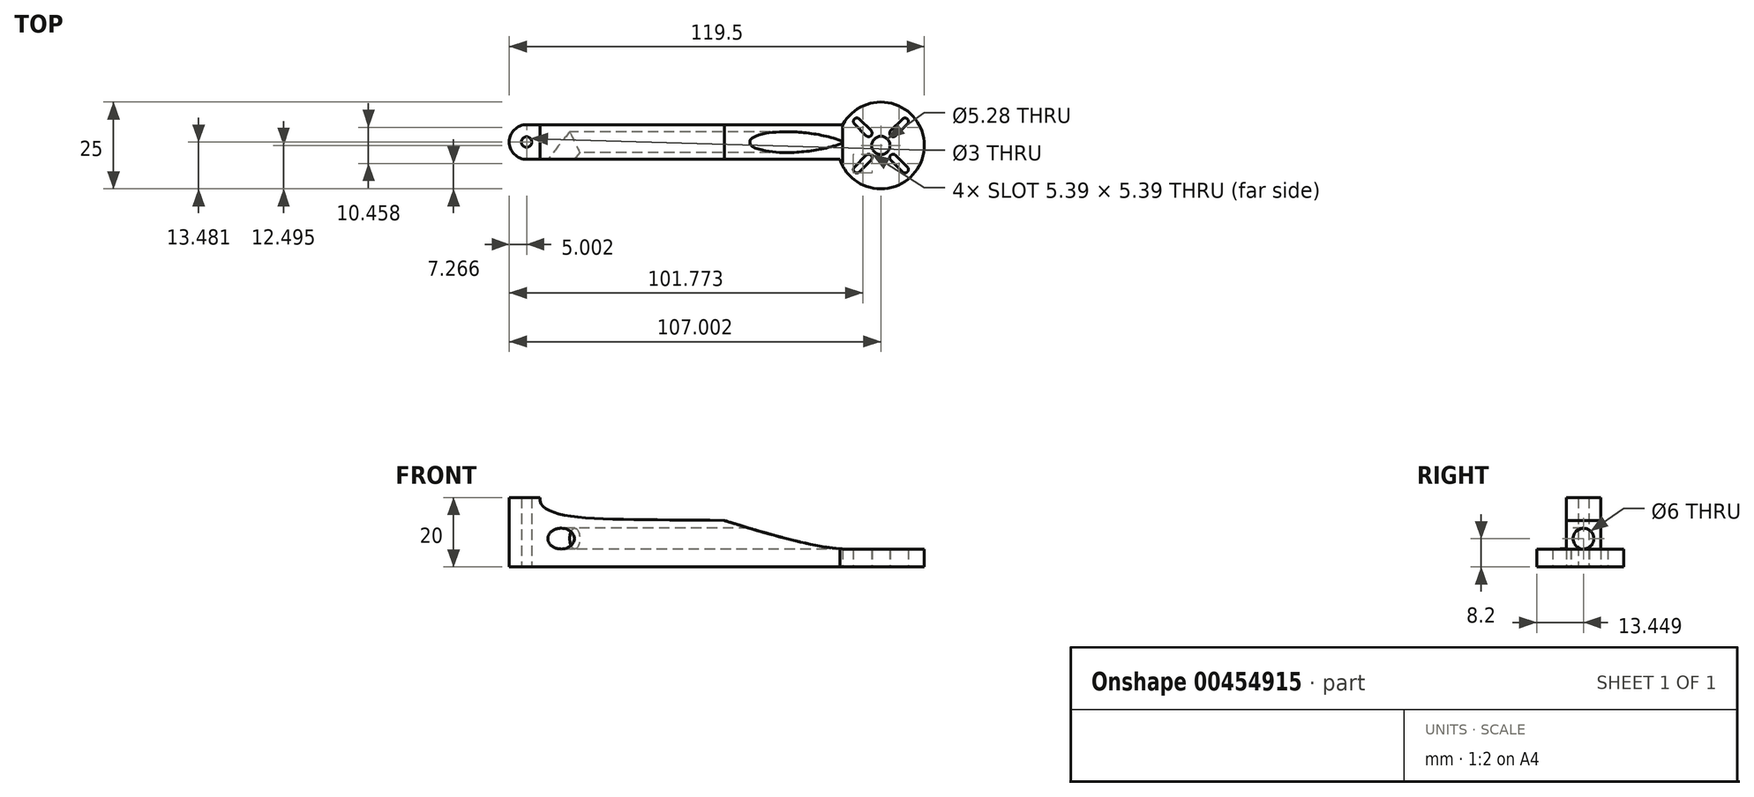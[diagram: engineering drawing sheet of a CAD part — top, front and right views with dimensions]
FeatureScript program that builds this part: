
annotation { "Feature Type Name" : "Feature", "Feature Type Description" : "" }
export const myFeature = defineFeature(function(context is Context, id is Id, definition is map)
    precondition{}
    {
        {
            var Q0;
            Q0=qCreatedBy(makeId("Top.planeOp"),FACE);
            var sketch = newSketch(context, id + "F0", { "sketchPlane" : qUnion([Q0])});
            skLineSegment(sketch, "E0", {"start": v(-139.16, 59.15) * mm, "end": v(-37.16, 59.15) * mm, "construction": true});
            skArc(sketch, "E1", {"start": v(-48.13, 53.17) * mm, "mid": v(-24.7, 60.23) * mm, "end": v(-49, 63.17) * mm});
            skLineSegment(sketch, "E2", {"start": v(-139.16, 63.17) * mm, "end": v(-49, 63.17) * mm});
            skLineSegment(sketch, "E3", {"start": v(-139.16, 53.17) * mm, "end": v(-48.13, 53.17) * mm});
            skCircle(sketch, "E4", {"center": v(-37.16, 59.15) * mm, "radius": 2.64 * mm});
            skArc(sketch, "E5.0.startCap", {"start": v(-44.79, 65.37) * mm, "mid": v(-44.79, 66.78) * mm, "end": v(-43.37, 66.78) * mm});
            skArc(sketch, "E5.0.endCap", {"start": v(-39.99, 63.4) * mm, "mid": v(-39.99, 61.98) * mm, "end": v(-41.4, 61.98) * mm});
            skLineSegment(sketch, "E5.0.left", {"start": v(-43.37, 66.78) * mm, "end": v(-39.99, 63.4) * mm});
            skLineSegment(sketch, "E5.0.right", {"start": v(-44.79, 65.37) * mm, "end": v(-41.4, 61.98) * mm});
            skLineSegment(sketch, "E6", {"start": v(-37.16, 59.15) * mm, "end": v(-37.16, 66.76) * mm, "construction": true});
            skArc(sketch, "E7.MirrorCS", {"start": v(-29.53, 65.37) * mm, "mid": v(-29.53, 66.78) * mm, "end": v(-30.94, 66.78) * mm});
            skArc(sketch, "E8.MirrorCS", {"start": v(-34.33, 63.4) * mm, "mid": v(-34.33, 61.98) * mm, "end": v(-32.92, 61.98) * mm});
            skLineSegment(sketch, "E9.MirrorCS", {"start": v(-29.53, 65.37) * mm, "end": v(-32.92, 61.98) * mm});
            skLineSegment(sketch, "E10.MirrorCS", {"start": v(-30.94, 66.78) * mm, "end": v(-34.33, 63.4) * mm});
            skLineSegment(sketch, "E11.MirrorCS", {"start": v(-30.94, 51.52) * mm, "end": v(-34.33, 54.91) * mm});
            skArc(sketch, "E12.MirrorCS", {"start": v(-29.53, 52.94) * mm, "mid": v(-29.53, 51.52) * mm, "end": v(-30.94, 51.52) * mm});
            skLineSegment(sketch, "E13.MirrorCS", {"start": v(-29.53, 52.94) * mm, "end": v(-32.92, 56.33) * mm});
            skArc(sketch, "E14.MirrorCS", {"start": v(-34.33, 54.91) * mm, "mid": v(-34.33, 56.33) * mm, "end": v(-32.92, 56.33) * mm});
            skLineSegment(sketch, "E15.MirrorCS", {"start": v(-44.79, 52.94) * mm, "end": v(-41.4, 56.33) * mm});
            skLineSegment(sketch, "E16.MirrorCS", {"start": v(-43.37, 51.52) * mm, "end": v(-39.99, 54.91) * mm});
            skArc(sketch, "E17.MirrorCS", {"start": v(-39.99, 54.91) * mm, "mid": v(-39.99, 56.33) * mm, "end": v(-41.4, 56.33) * mm});
            skArc(sketch, "E18.MirrorCS", {"start": v(-44.79, 52.94) * mm, "mid": v(-44.79, 51.52) * mm, "end": v(-43.37, 51.52) * mm});
            skLineSegment(sketch, "E19", {"start": v(-37.16, 59.15) * mm, "end": v(-44.76, 66.76) * mm, "construction": true});
            skLineSegment(sketch, "E20", {"start": v(-139.16, 53.17) * mm, "end": v(-139.16, 63.17) * mm, "construction": true});
            skPoint(sketch, "E21", {"position": v(-139.16, 58.17) * mm});
            skArc(sketch, "E22", {"start": v(-139.16, 53.17) * mm, "mid": v(-144.16, 58.17) * mm, "end": v(-139.16, 63.17) * mm});
            skCircle(sketch, "E23", {"center": v(-139.16, 58.17) * mm, "radius": 1.5 * mm});
            skSolve(sketch);
        }
        {
            var Q0;
            Q0=qSketchRegion(id+"F0",true);
            extrude(context, id + "F1", {"entities" : qUnion([Q0]), "depth" : 20 * mm});
        }
        {
            var Q0;
            Q0=makeQuery(id+"F1.opExtrude","SWEPT_FACE",FACE,{"disambiguationData":[OSD([sQuery(id+"F0.wireOp",EDGE,"E3")])]});
            var sketch = newSketch(context, id + "F2", { "sketchPlane" : qUnion([Q0])});
            skFitSpline(sketch, "E24", {"points": [v(-48.13, 5.2) * mm, v(-101.02, 20) * mm], "startDerivative": vector(-37.65, 1.6) * mm, "endDerivative": vector(-23.18, 9.57) * mm});
            skLineSegment(sketch, "E25", {"start": v(-48.13, 5.2) * mm, "end": v(66.1, 5.2) * mm});
            skLineSegment(sketch, "E26", {"start": v(66.1, 5.2) * mm, "end": v(64.34, 23.02) * mm});
            skLineSegment(sketch, "E27", {"start": v(64.34, 23.02) * mm, "end": v(-14.17, 23.97) * mm});
            skLineSegment(sketch, "E28", {"start": v(-14.17, 23.97) * mm, "end": v(-21.08, 20) * mm});
            skLineSegment(sketch, "E29", {"start": v(-48.13, 13.43) * mm, "end": v(-82.25, 13.43) * mm});
            skLineSegment(sketch, "E30", {"start": v(-48.13, 13.43) * mm, "end": v(-48.13, 24.34) * mm});
            skLineSegment(sketch, "E31", {"start": v(-48.13, 24.34) * mm, "end": v(-21.08, 20) * mm});
            skSolve(sketch);
        }
        {
            var Q0;
            Q0=qSketchRegion(id+"F2",true);
            extrude(context, id + "F3", {"entities" : qUnion([Q0]), "operationType" : NewBodyOperationType.REMOVE, "oppositeDirection" : true, "depth" : 25 * mm, "hasSecondDirection" : true, "secondDirectionOppositeDirection" : false, "secondDirectionDepth" : 25 * mm});
        }
        {
            var Q0;
            Q0=makeQuery(id+"F3.boolean.opBoolean","COPY",FACE,{"derivedFrom":makeQuery(id+"F3.opExtrude","SWEPT_FACE",FACE,{"disambiguationData":[OSD([sQuery(id+"F2.wireOp",EDGE,"E25")])]})});
            var sketch = newSketch(context, id + "F4", { "sketchPlane" : qUnion([Q0])});
            skLineSegment(sketch, "E32", {"start": v(-86.71, 58.17) * mm, "end": v(-61.2, 58.17) * mm});
            skLineSegment(sketch, "E33", {"start": v(-86.71, 58.17) * mm, "end": v(-125.32, 58.17) * mm});
            skLineSegment(sketch, "E34", {"start": v(-125.32, 58.17) * mm, "end": v(-138.96, 75.4) * mm});
            skSolve(sketch);
        }
        {
            var Q0;
            Q0=makeQuery(id+"F3.boolean.opBoolean","COPY",EDGE,{"derivedFrom":makeQuery(id+"F3.opExtrude","SWEPT_EDGE",EDGE,{"disambiguationData":[OSD([sQuery(id+"F0.wireOp",EDGE,"E1"),sQuery(id+"F0.wireOp",EDGE,"E3"),sQuery(id+"F2.wireOp",EDGE,"E24"),sQuery(id+"F2.wireOp",EDGE,"E25")])]})});
            cPlane(context, id + "F5", {"entities" : qUnion([Q0]), "cplaneType" : CPlaneType.LINE_ANGLE, "offset" : 25 * mm, "angle" : 90 * degree, "width" : 150 * mm, "height" : 150 * mm});
        }
        {
            var Q0;
            Q0=qCreatedBy(id+"F5.planeOp",FACE);
            var sketch = newSketch(context, id + "F6", { "sketchPlane" : qUnion([Q0])});
            skLineSegment(sketch, "E35.0", {"start": v(65.14, 5.2) * mm, "end": v(53.17, 5.2) * mm, "construction": true});
            skCircle(sketch, "E36", {"center": v(58.2, 8.2) * mm, "radius": 3 * mm});
            skSolve(sketch);
        }
        {
            var Q0;
            Q0=qSketchRegion(id+"F6",true);
            var Q1;
            Q1=qConstructionFilter(qBodyType(qCreatedBy(id+"F4",EDGE),BodyType.WIRE),ConstructionObject.NO);
            sweep(context, id + "F7", {"operationType" : NewBodyOperationType.REMOVE, "profiles" : qUnion([Q0]), "path" : qUnion([Q1])});
        }
        {
            var Q0;
            Q0=makeQuery(id+"F1.opExtrude","SWEPT_FACE",FACE,{"disambiguationData":[OSD([sQuery(id+"F0.wireOp",EDGE,"E3")])]});
            var sketch = newSketch(context, id + "F8", { "sketchPlane" : qUnion([Q0])});
            skPoint(sketch, "E37.0", {"position": v(-82.25, 13.43) * mm});
            skFitSpline(sketch, "E38", {"points": [v(-82.25, 13.43) * mm, v(-135.35, 20) * mm], "startDerivative": vector(-96, 1.58) * mm, "endDerivative": vector(1.3, 22.57) * mm});
            skLineSegment(sketch, "E39", {"start": v(-82.25, 13.43) * mm, "end": v(-32.97, 11.71) * mm});
            skLineSegment(sketch, "E40", {"start": v(-32.97, 11.71) * mm, "end": v(-32.97, 37.38) * mm});
            skLineSegment(sketch, "E41", {"start": v(-32.97, 37.38) * mm, "end": v(-135.35, 20) * mm});
            skSolve(sketch);
        }
        {
            var Q0;
            Q0=qSketchRegion(id+"F8",true);
            extrude(context, id + "F9", {"entities" : qUnion([Q0]), "operationType" : NewBodyOperationType.REMOVE, "oppositeDirection" : true, "depth" : 25 * mm});
        }
        {
            var Q0;
            Q0=makeQuery(id+"F1.opExtrude","SWEPT_BODY",BODY,{"disambiguationData":[OSD([sQuery(id+"F0.wireOp",EDGE,"E1"),sQuery(id+"F0.wireOp",EDGE,"E2"),sQuery(id+"F0.wireOp",EDGE,"E3"),sQuery(id+"F0.wireOp",EDGE,"E4"),sQuery(id+"F0.wireOp",EDGE,"E5.0.startCap"),sQuery(id+"F0.wireOp",EDGE,"E5.0.endCap"),sQuery(id+"F0.wireOp",EDGE,"E5.0.left"),sQuery(id+"F0.wireOp",EDGE,"E5.0.right"),sQuery(id+"F0.wireOp",EDGE,"E7.MirrorCS"),sQuery(id+"F0.wireOp",EDGE,"E8.MirrorCS"),sQuery(id+"F0.wireOp",EDGE,"E9.MirrorCS"),sQuery(id+"F0.wireOp",EDGE,"E10.MirrorCS"),sQuery(id+"F0.wireOp",EDGE,"E11.MirrorCS"),sQuery(id+"F0.wireOp",EDGE,"E12.MirrorCS"),sQuery(id+"F0.wireOp",EDGE,"E13.MirrorCS"),sQuery(id+"F0.wireOp",EDGE,"E14.MirrorCS"),sQuery(id+"F0.wireOp",EDGE,"E15.MirrorCS"),sQuery(id+"F0.wireOp",EDGE,"E16.MirrorCS"),sQuery(id+"F0.wireOp",EDGE,"E17.MirrorCS"),sQuery(id+"F0.wireOp",EDGE,"E18.MirrorCS"),sQuery(id+"F0.wireOp",EDGE,"E22"),sQuery(id+"F0.wireOp",EDGE,"E23")])]});
            var Q1;
            Q1=qCreatedBy(makeId("Front.planeOp"),FACE);
            mirror(context, id + "F10", {"entities" : qUnion([Q0]), "mirrorPlane" : qUnion([Q1])});
        }
        {
            var Q0;
            Q0=makeQuery(id+"F1.opExtrude","CAP_FACE",FACE,{"disambiguationData":[OSD([sQuery(id+"F0.wireOp",EDGE,"E1"),sQuery(id+"F0.wireOp",EDGE,"E2"),sQuery(id+"F0.wireOp",EDGE,"E3"),sQuery(id+"F0.wireOp",EDGE,"E4"),sQuery(id+"F0.wireOp",EDGE,"E5.0.startCap"),sQuery(id+"F0.wireOp",EDGE,"E5.0.endCap"),sQuery(id+"F0.wireOp",EDGE,"E5.0.left"),sQuery(id+"F0.wireOp",EDGE,"E5.0.right"),sQuery(id+"F0.wireOp",EDGE,"E7.MirrorCS"),sQuery(id+"F0.wireOp",EDGE,"E8.MirrorCS"),sQuery(id+"F0.wireOp",EDGE,"E9.MirrorCS"),sQuery(id+"F0.wireOp",EDGE,"E10.MirrorCS"),sQuery(id+"F0.wireOp",EDGE,"E11.MirrorCS"),sQuery(id+"F0.wireOp",EDGE,"E12.MirrorCS"),sQuery(id+"F0.wireOp",EDGE,"E13.MirrorCS"),sQuery(id+"F0.wireOp",EDGE,"E14.MirrorCS"),sQuery(id+"F0.wireOp",EDGE,"E15.MirrorCS"),sQuery(id+"F0.wireOp",EDGE,"E16.MirrorCS"),sQuery(id+"F0.wireOp",EDGE,"E17.MirrorCS"),sQuery(id+"F0.wireOp",EDGE,"E18.MirrorCS"),sQuery(id+"F0.wireOp",EDGE,"E22"),sQuery(id+"F0.wireOp",EDGE,"E23")])],"isStart":false});
            var sketch = newSketch(context, id + "F11", { "sketchPlane" : qUnion([Q0])});
            skLineSegment(sketch, "E42.bottom", {"start": v(-152.39, 12.15) * mm, "end": v(-2.77, 12.15) * mm});
            skLineSegment(sketch, "E42.top", {"start": v(-152.39, 131.84) * mm, "end": v(-2.77, 131.84) * mm});
            skLineSegment(sketch, "E42.left", {"start": v(-152.39, 12.15) * mm, "end": v(-152.39, 131.84) * mm});
            skLineSegment(sketch, "E42.right", {"start": v(-2.77, 12.15) * mm, "end": v(-2.77, 131.84) * mm});
            skSolve(sketch);
        }
        {
            var Q0;
            Q0 = qSketchRegion(id + "F11", true);
            extrude(context, id + "F12", {"entities" : qUnion([Q0]), "operationType" : NewBodyOperationType.REMOVE, "oppositeDirection" : true, "depth" : 25 * mm});
        }
    });
